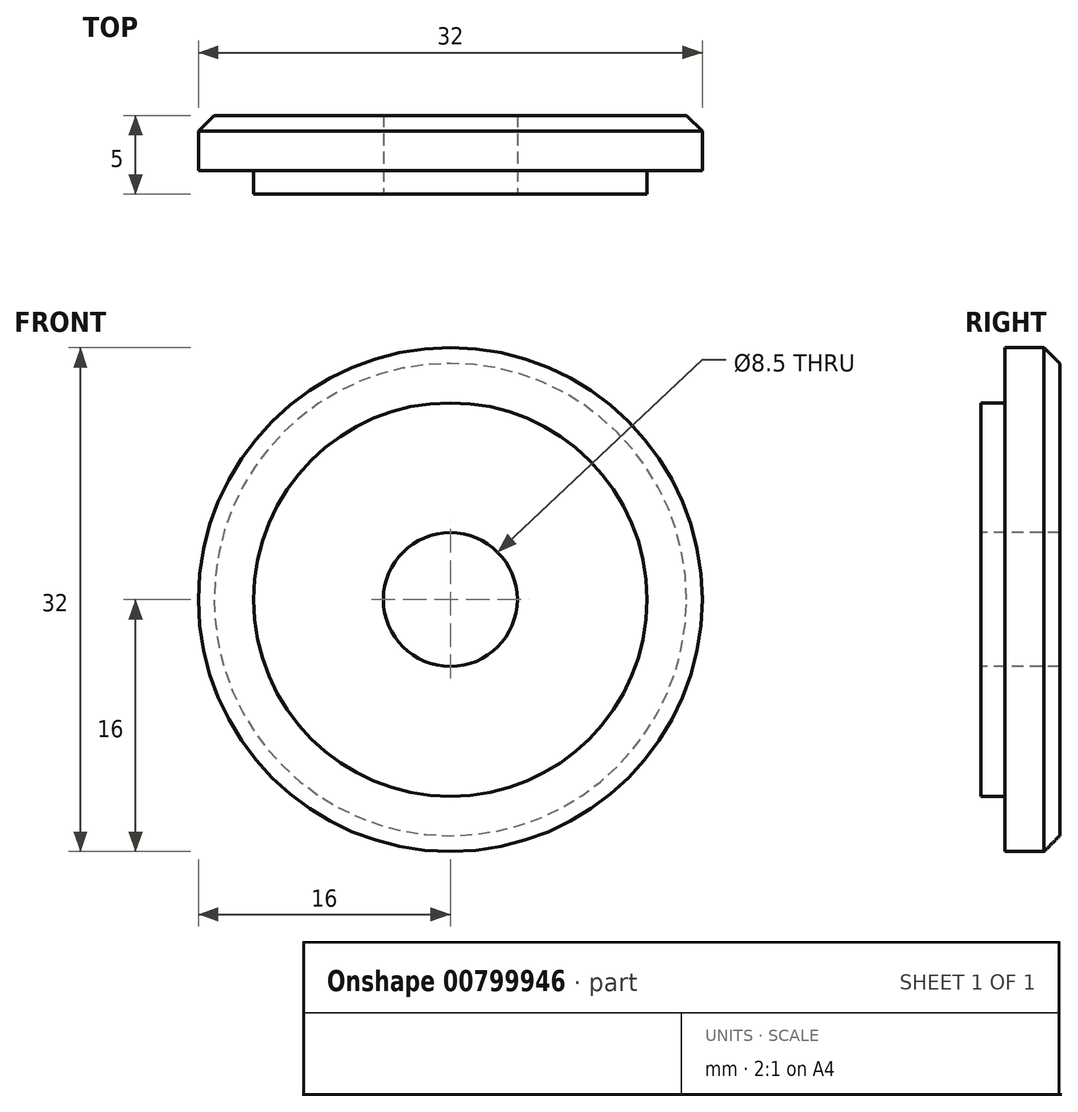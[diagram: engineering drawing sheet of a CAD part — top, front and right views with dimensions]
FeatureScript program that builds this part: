
annotation { "Feature Type Name" : "Feature", "Feature Type Description" : "" }
export const myFeature = defineFeature(function(context is Context, id is Id, definition is map)
    precondition{}
    {
        {
            var Q0;
            Q0=qCreatedBy(makeId("Front.planeOp"),FACE);
            var sketch = newSketch(context, id + "F0", { "sketchPlane" : qUnion([Q0])});
            skCircle(sketch, "E0", {"center": v(0, 0) * mm, "radius": 16 * mm});
            skSolve(sketch);
        }
        {
            var Q0;
            Q0 = qSketchRegion(id + "F0", true);
            extrude(context, id + "F1", {"entities" : qUnion([Q0]), "depth" : 5 * mm, "offsetDistance" : 25 * mm});
        }
        {
            var Q0;
            Q0=makeQuery(id+"F1.opExtrude","CAP_FACE",FACE,{"disambiguationData":[OSD([sQuery(id+"F0.wireOp",EDGE,"E0")])],"isStart":false});
            var sketch = newSketch(context, id + "F2", { "sketchPlane" : qUnion([Q0])});
            skCircle(sketch, "E1", {"center": v(0, 0) * mm, "radius": 12.5 * mm});
            skCircle(sketch, "E2", {"center": v(0, 0) * mm, "radius": 23.3 * mm});
            skSolve(sketch);
        }
        {
            var Q0;
            Q0 = qSketchRegion(id + "F2", true);
            extrude(context, id + "F3", {"entities" : qUnion([Q0]), "operationType" : NewBodyOperationType.REMOVE, "oppositeDirection" : true, "depth" : 1.5 * mm, "offsetDistance" : 25 * mm});
        }
        {
            var Q0;
            Q0=makeQuery(id+"F1.opExtrude","CAP_EDGE",EDGE,{"disambiguationData":[OSD([sQuery(id+"F0.wireOp",EDGE,"E0")])],"isStart":true});
            chamfer(context, id + "F4", {"entities" : qUnion([Q0]), "width" : 1 * mm, "tangentPropagation" : true});
        }
        {
            var Q0;
            Q0=makeQuery(id+"F1.opExtrude","CAP_FACE",FACE,{"disambiguationData":[OSD([sQuery(id+"F0.wireOp",EDGE,"E0")])],"isStart":false});
            var sketch = newSketch(context, id + "F5", { "sketchPlane" : qUnion([Q0])});
            skCircle(sketch, "E3", {"center": v(0, 0) * mm, "radius": 4.25 * mm});
            skSolve(sketch);
        }
        {
            var Q0;
            Q0 = qSketchRegion(id + "F5", true);
            extrude(context, id + "F6", {"entities" : qUnion([Q0]), "operationType" : NewBodyOperationType.REMOVE, "oppositeDirection" : true, "depth" : 25 * mm, "offsetDistance" : 25 * mm});
        }
    });
